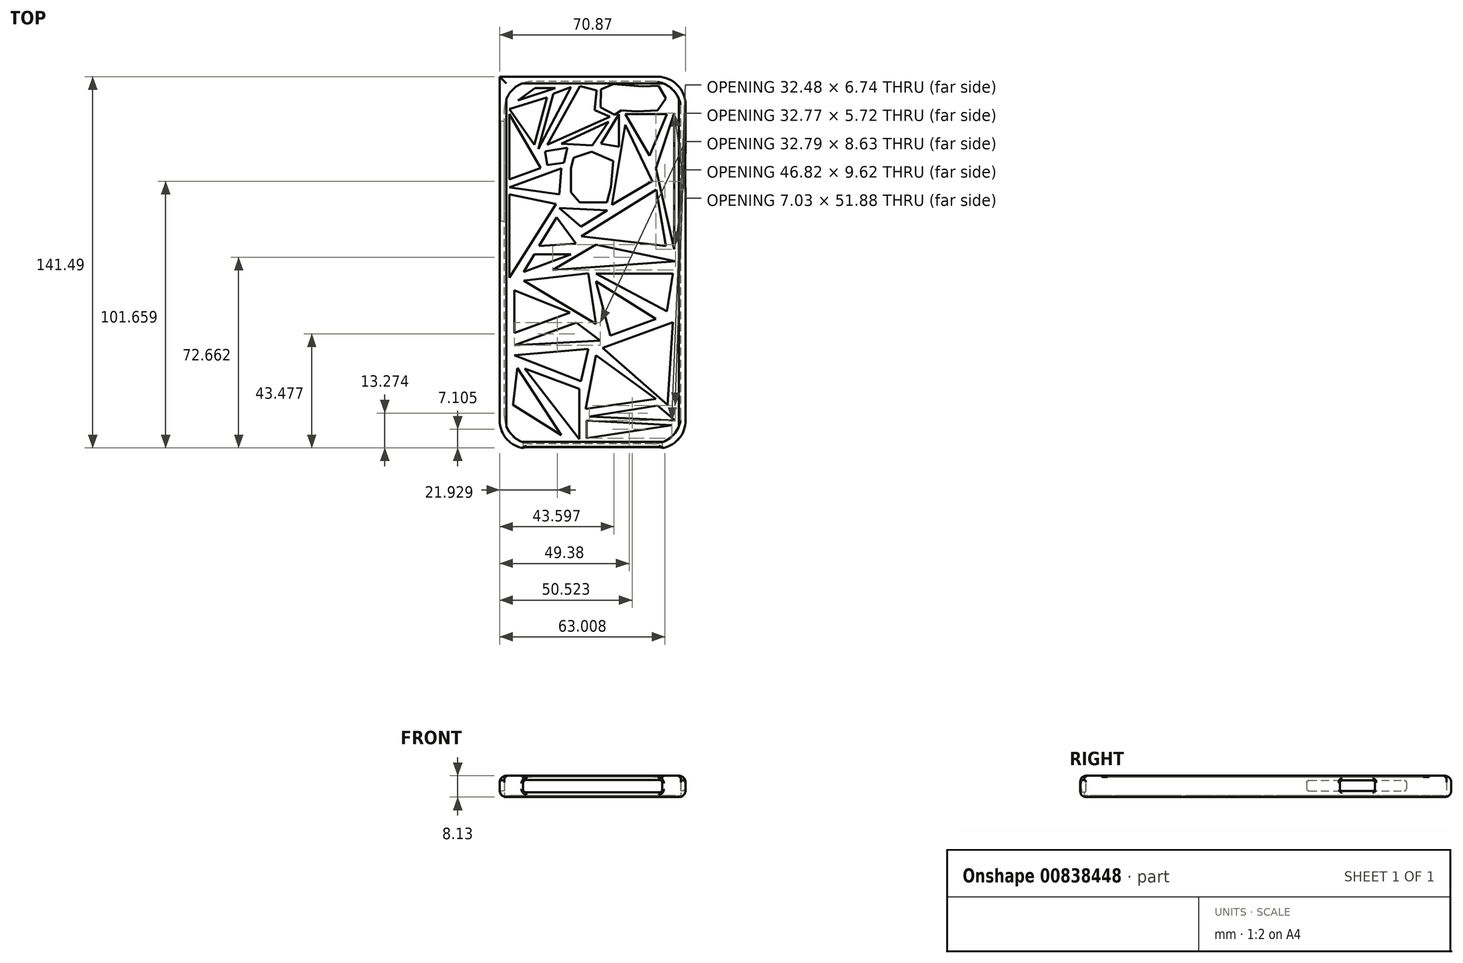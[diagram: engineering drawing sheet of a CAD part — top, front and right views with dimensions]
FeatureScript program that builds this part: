
annotation { "Feature Type Name" : "Feature", "Feature Type Description" : "" }
export const myFeature = defineFeature(function(context is Context, id is Id, definition is map)
    precondition{}
    {
        {
            var Q0;
            Q0=qCreatedBy(makeId("Top.planeOp"),FACE);
            var sketch = newSketch(context, id + "F0", { "sketchPlane" : qUnion([Q0])});
            skLineSegment(sketch, "E0.bottom", {"start": v(0, 0) * mm, "end": v(70.87, 0) * mm});
            skLineSegment(sketch, "E0.top", {"start": v(0, -141.73) * mm, "end": v(70.87, -141.73) * mm});
            skLineSegment(sketch, "E0.left", {"start": v(0, 0) * mm, "end": v(0, -141.73) * mm});
            skLineSegment(sketch, "E0.right", {"start": v(70.87, 0) * mm, "end": v(70.87, -141.73) * mm});
            skLineSegment(sketch, "E1.bottom", {"start": v(0, 0) * mm, "end": v(66.75, 0) * mm});
            skLineSegment(sketch, "E1.left", {"start": v(0, 0) * mm, "end": v(0, -137.57) * mm});
            skLineSegment(sketch, "E2.bottom", {"start": v(69.09, -139.95) * mm, "end": v(1.78, -139.95) * mm});
            skLineSegment(sketch, "E2.top", {"start": v(69.09, -1.78) * mm, "end": v(1.78, -1.78) * mm});
            skLineSegment(sketch, "E2.left", {"start": v(69.09, -139.95) * mm, "end": v(69.09, -1.78) * mm});
            skLineSegment(sketch, "E2.right", {"start": v(1.78, -139.95) * mm, "end": v(1.78, -1.78) * mm});
            skPoint(sketch, "E2.middle", {"position": v(35.43, -70.87) * mm});
            skLineSegment(sketch, "E3.0", {"start": v(21.2, -4.27) * mm, "end": v(7, -8.96) * mm});
            skLineSegment(sketch, "E3.1", {"start": v(7, -8.96) * mm, "end": v(13.43, -4.27) * mm});
            skLineSegment(sketch, "E3.2", {"start": v(13.43, -4.27) * mm, "end": v(21.2, -4.27) * mm});
            skPoint(sketch, "E3.0.midPoint", {"position": v(14.1, -6.62) * mm});
            skLineSegment(sketch, "E4", {"start": v(3.66, -12.3) * mm, "end": v(17.98, -7.89) * mm});
            skLineSegment(sketch, "E5", {"start": v(17.98, -7.89) * mm, "end": v(13.16, -25.95) * mm});
            skLineSegment(sketch, "E6", {"start": v(13.16, -25.95) * mm, "end": v(3.66, -12.3) * mm});
            skLineSegment(sketch, "E7", {"start": v(3.66, -14.2) * mm, "end": v(3.66, -39.11) * mm});
            skLineSegment(sketch, "E8", {"start": v(3.66, -39.11) * mm, "end": v(15.66, -34.74) * mm});
            skLineSegment(sketch, "E9", {"start": v(15.66, -34.74) * mm, "end": v(3.66, -14.2) * mm});
            skLineSegment(sketch, "E10", {"start": v(14.77, -27.56) * mm, "end": v(20.4, -6.45) * mm});
            skLineSegment(sketch, "E11", {"start": v(20.4, -6.45) * mm, "end": v(27.18, -3.98) * mm});
            skLineSegment(sketch, "E12", {"start": v(27.18, -3.98) * mm, "end": v(14.77, -27.56) * mm});
            skLineSegment(sketch, "E13", {"start": v(23.44, -25.52) * mm, "end": v(35.27, -26.22) * mm});
            skLineSegment(sketch, "E14", {"start": v(35.27, -26.22) * mm, "end": v(41.5, -17.2) * mm});
            skLineSegment(sketch, "E15", {"start": v(41.5, -17.2) * mm, "end": v(23.44, -25.52) * mm});
            skLineSegment(sketch, "E16", {"start": v(45.4, -14.2) * mm, "end": v(45.4, -26.67) * mm});
            skLineSegment(sketch, "E17", {"start": v(45.4, -26.67) * mm, "end": v(38.58, -25.58) * mm});
            skLineSegment(sketch, "E18", {"start": v(38.58, -25.58) * mm, "end": v(45.4, -14.2) * mm});
            skLineSegment(sketch, "E19", {"start": v(47.85, -14.2) * mm, "end": v(57.17, -30.16) * mm});
            skLineSegment(sketch, "E20", {"start": v(57.17, -30.16) * mm, "end": v(63.8, -14.25) * mm});
            skLineSegment(sketch, "E21", {"start": v(63.8, -14.25) * mm, "end": v(47.85, -14.2) * mm});
            skLineSegment(sketch, "E22", {"start": v(47.85, -18.22) * mm, "end": v(42.74, -48.7) * mm});
            skLineSegment(sketch, "E23", {"start": v(42.74, -48.7) * mm, "end": v(58.17, -39.69) * mm});
            skLineSegment(sketch, "E24", {"start": v(58.17, -39.69) * mm, "end": v(47.85, -18.22) * mm});
            skLineSegment(sketch, "E25", {"start": v(59.5, -34.98) * mm, "end": v(66.53, -65.77) * mm});
            skLineSegment(sketch, "E26", {"start": v(66.53, -65.77) * mm, "end": v(66.53, -13.9) * mm});
            skLineSegment(sketch, "E27", {"start": v(66.53, -13.9) * mm, "end": v(59.5, -34.98) * mm});
            skLineSegment(sketch, "E28", {"start": v(59.62, -43.08) * mm, "end": v(31.16, -60.86) * mm});
            skLineSegment(sketch, "E29", {"start": v(31.16, -60.86) * mm, "end": v(63.41, -64.56) * mm});
            skLineSegment(sketch, "E30", {"start": v(63.41, -64.56) * mm, "end": v(59.62, -43.08) * mm});
            skLineSegment(sketch, "E31", {"start": v(23.44, -34.98) * mm, "end": v(3.66, -42.2) * mm});
            skLineSegment(sketch, "E32", {"start": v(3.66, -42.2) * mm, "end": v(22.67, -44.83) * mm});
            skLineSegment(sketch, "E33", {"start": v(22.67, -44.83) * mm, "end": v(23.44, -34.98) * mm});
            skLineSegment(sketch, "E34", {"start": v(3.66, -44.83) * mm, "end": v(3.66, -76.54) * mm});
            skLineSegment(sketch, "E35", {"start": v(3.66, -76.54) * mm, "end": v(21.46, -48.57) * mm});
            skLineSegment(sketch, "E36", {"start": v(21.46, -48.57) * mm, "end": v(3.66, -44.83) * mm});
            skLineSegment(sketch, "E37", {"start": v(27.18, -67.68) * mm, "end": v(13.21, -67.68) * mm});
            skLineSegment(sketch, "E38", {"start": v(13.21, -67.68) * mm, "end": v(9.15, -74.46) * mm});
            skLineSegment(sketch, "E39", {"start": v(9.15, -74.46) * mm, "end": v(27.18, -67.68) * mm});
            skLineSegment(sketch, "E40", {"start": v(36.66, -64.02) * mm, "end": v(20.19, -73.64) * mm});
            skLineSegment(sketch, "E41", {"start": v(20.19, -73.64) * mm, "end": v(67, -70.4) * mm});
            skLineSegment(sketch, "E42", {"start": v(67, -70.4) * mm, "end": v(36.66, -64.02) * mm});
            skLineSegment(sketch, "E43", {"start": v(63.76, -89.4) * mm, "end": v(36.76, -75.11) * mm});
            skLineSegment(sketch, "E44", {"start": v(36.76, -75.11) * mm, "end": v(65.98, -75.11) * mm});
            skLineSegment(sketch, "E45", {"start": v(63.76, -89.4) * mm, "end": v(65.98, -75.11) * mm});
            skLineSegment(sketch, "E46", {"start": v(36.75, -77.91) * mm, "end": v(59.5, -92.38) * mm});
            skLineSegment(sketch, "E47", {"start": v(59.5, -92.38) * mm, "end": v(42.21, -98.68) * mm});
            skLineSegment(sketch, "E48", {"start": v(42.21, -98.68) * mm, "end": v(36.75, -77.91) * mm});
            skLineSegment(sketch, "E49", {"start": v(33.77, -74.94) * mm, "end": v(9.15, -77.75) * mm});
            skLineSegment(sketch, "E50", {"start": v(9.15, -77.75) * mm, "end": v(36.75, -94.26) * mm});
            skLineSegment(sketch, "E51", {"start": v(36.75, -94.26) * mm, "end": v(33.77, -74.94) * mm});
            skLineSegment(sketch, "E52", {"start": v(5.53, -81.36) * mm, "end": v(5.53, -97.7) * mm});
            skLineSegment(sketch, "E53", {"start": v(5.53, -97.7) * mm, "end": v(26.84, -89.93) * mm});
            skLineSegment(sketch, "E54", {"start": v(26.84, -89.93) * mm, "end": v(5.53, -81.36) * mm});
            skLineSegment(sketch, "E55", {"start": v(29.2, -93.7) * mm, "end": v(5.53, -102.33) * mm});
            skLineSegment(sketch, "E56", {"start": v(5.53, -102.33) * mm, "end": v(38.32, -100.63) * mm});
            skLineSegment(sketch, "E57", {"start": v(38.32, -100.63) * mm, "end": v(29.2, -93.7) * mm});
            skLineSegment(sketch, "E58", {"start": v(65.98, -93.63) * mm, "end": v(39.3, -103.36) * mm});
            skLineSegment(sketch, "E59", {"start": v(39.3, -103.36) * mm, "end": v(64.02, -125.13) * mm});
            skLineSegment(sketch, "E60", {"start": v(64.02, -125.13) * mm, "end": v(65.98, -93.63) * mm});
            skLineSegment(sketch, "E61", {"start": v(36.75, -106.12) * mm, "end": v(32.81, -126.58) * mm});
            skLineSegment(sketch, "E62", {"start": v(32.81, -126.58) * mm, "end": v(59.5, -122.77) * mm});
            skLineSegment(sketch, "E63", {"start": v(59.5, -122.77) * mm, "end": v(36.75, -106.12) * mm});
            skLineSegment(sketch, "E64", {"start": v(60.13, -125.36) * mm, "end": v(34.14, -129.48) * mm});
            skLineSegment(sketch, "E65", {"start": v(34.14, -129.48) * mm, "end": v(66.9, -131.07) * mm});
            skLineSegment(sketch, "E66", {"start": v(66.9, -131.07) * mm, "end": v(60.13, -125.36) * mm});
            skLineSegment(sketch, "E67", {"start": v(33.77, -103.71) * mm, "end": v(5.53, -106.12) * mm});
            skLineSegment(sketch, "E68", {"start": v(5.53, -106.12) * mm, "end": v(31.04, -116.01) * mm});
            skLineSegment(sketch, "E69", {"start": v(31.04, -116.01) * mm, "end": v(33.77, -103.71) * mm});
            skLineSegment(sketch, "E70", {"start": v(6.74, -110.94) * mm, "end": v(5.12, -125.08) * mm});
            skLineSegment(sketch, "E71", {"start": v(5.12, -125.08) * mm, "end": v(23.44, -136.7) * mm});
            skLineSegment(sketch, "E72", {"start": v(23.44, -136.7) * mm, "end": v(6.74, -110.94) * mm});
            skLineSegment(sketch, "E73", {"start": v(9.52, -111.2) * mm, "end": v(30.36, -138.16) * mm});
            skLineSegment(sketch, "E74", {"start": v(30.36, -138.16) * mm, "end": v(30.36, -118.96) * mm});
            skLineSegment(sketch, "E75", {"start": v(30.36, -118.96) * mm, "end": v(9.52, -111.2) * mm});
            skPoint(sketch, "E76.middle", {"position": v(51.66, -7.81) * mm});
            skPoint(sketch, "E76.middle.positionSnap0", {"position": v(53.2, -9.7) * mm});
            skPoint(sketch, "E76.centerSnap0", {"position": v(51.66, -10.15) * mm});
            skLineSegment(sketch, "E77", {"start": v(30.6, -3.5) * mm, "end": v(18.11, -25.94) * mm});
            skLineSegment(sketch, "E78", {"start": v(18.11, -25.94) * mm, "end": v(41.99, -15.27) * mm});
            skLineSegment(sketch, "E79", {"start": v(41.99, -15.27) * mm, "end": v(36.18, -12.73) * mm});
            skLineSegment(sketch, "E80", {"start": v(36.18, -12.73) * mm, "end": v(36.9, -5.25) * mm});
            skLineSegment(sketch, "E81", {"start": v(36.9, -5.25) * mm, "end": v(30.6, -3.5) * mm});
            skLineSegment(sketch, "E82", {"start": v(38.56, -4.85) * mm, "end": v(43.3, -2.82) * mm});
            skLineSegment(sketch, "E83", {"start": v(43.3, -2.82) * mm, "end": v(54.53, -3.7) * mm});
            skLineSegment(sketch, "E84", {"start": v(54.53, -3.7) * mm, "end": v(60.52, -3.44) * mm});
            skLineSegment(sketch, "E85", {"start": v(60.52, -3.44) * mm, "end": v(63.38, -8.25) * mm});
            skLineSegment(sketch, "E86", {"start": v(63.38, -8.25) * mm, "end": v(60.18, -12.89) * mm});
            skLineSegment(sketch, "E87", {"start": v(60.18, -12.89) * mm, "end": v(52.28, -13.27) * mm});
            skLineSegment(sketch, "E88", {"start": v(52.28, -13.27) * mm, "end": v(46.4, -12.8) * mm});
            skLineSegment(sketch, "E89", {"start": v(46.4, -12.8) * mm, "end": v(43.82, -14.42) * mm});
            skLineSegment(sketch, "E90", {"start": v(43.82, -14.42) * mm, "end": v(38.46, -11.7) * mm});
            skLineSegment(sketch, "E91", {"start": v(38.46, -11.7) * mm, "end": v(38.56, -4.85) * mm});
            skLineSegment(sketch, "E92", {"start": v(0, -141.73) * mm, "end": v(0, 0) * mm});
            skLineSegment(sketch, "E93", {"start": v(70.87, -34.36) * mm, "end": v(43.69, -34.36) * mm, "construction": true});
            skLineSegment(sketch, "E94", {"start": v(43.69, -34.36) * mm, "end": v(43.69, -28.24) * mm, "construction": true});
            skLineSegment(sketch, "E95", {"start": v(33.38, -28.58) * mm, "end": v(43.69, -28.58) * mm, "construction": true});
            skLineSegment(sketch, "E96", {"start": v(43.69, -28.58) * mm, "end": v(43.69, -47.87) * mm, "construction": true});
            skLineSegment(sketch, "E97", {"start": v(43.69, -47.87) * mm, "end": v(27.18, -47.87) * mm, "construction": true});
            skLineSegment(sketch, "E98", {"start": v(27.18, -47.87) * mm, "end": v(27.18, -28.58) * mm, "construction": true});
            skLineSegment(sketch, "E99", {"start": v(27.18, -28.58) * mm, "end": v(33.38, -28.58) * mm, "construction": true});
            skLineSegment(sketch, "E100", {"start": v(17.23, -28.41) * mm, "end": v(25.81, -27.1) * mm});
            skLineSegment(sketch, "E101", {"start": v(25.81, -27.1) * mm, "end": v(24.5, -32.7) * mm});
            skLineSegment(sketch, "E102", {"start": v(24.5, -32.7) * mm, "end": v(18.1, -33.67) * mm});
            skLineSegment(sketch, "E103", {"start": v(18.1, -33.67) * mm, "end": v(17.23, -28.41) * mm});
            skLineSegment(sketch, "E104", {"start": v(41.06, -50.92) * mm, "end": v(22.75, -50.05) * mm});
            skLineSegment(sketch, "E105", {"start": v(22.75, -50.05) * mm, "end": v(30.98, -57.14) * mm});
            skLineSegment(sketch, "E106", {"start": v(30.98, -57.14) * mm, "end": v(41.06, -50.92) * mm});
            skLineSegment(sketch, "E107", {"start": v(27.18, -47.87) * mm, "end": v(27.18, -40.15) * mm});
            skLineSegment(sketch, "E108", {"start": v(27.18, -40.15) * mm, "end": v(27.18, -40.15) * mm});
            skLineSegment(sketch, "E109", {"start": v(27.18, -40.15) * mm, "end": v(27.18, -34.8) * mm});
            skLineSegment(sketch, "E110", {"start": v(27.18, -34.8) * mm, "end": v(27.18, -29.73) * mm});
            skLineSegment(sketch, "E111", {"start": v(35.02, -28.58) * mm, "end": v(43.34, -32.12) * mm});
            skLineSegment(sketch, "E112", {"start": v(43.34, -32.12) * mm, "end": v(42.38, -42.06) * mm});
            skLineSegment(sketch, "E113", {"start": v(42.38, -42.06) * mm, "end": v(40.85, -47.87) * mm});
            skLineSegment(sketch, "E114", {"start": v(40.85, -47.87) * mm, "end": v(30.42, -47.87) * mm});
            skLineSegment(sketch, "E115", {"start": v(30.42, -47.87) * mm, "end": v(27.18, -44.01) * mm});
            skLineSegment(sketch, "E116", {"start": v(27.18, -44.01) * mm, "end": v(28.5, -38.82) * mm});
            skLineSegment(sketch, "E117", {"start": v(28.5, -38.82) * mm, "end": v(27.18, -34.8) * mm});
            skLineSegment(sketch, "E118", {"start": v(27.18, -34.8) * mm, "end": v(28.23, -30.8) * mm});
            skLineSegment(sketch, "E119", {"start": v(28.23, -30.8) * mm, "end": v(35.02, -28.58) * mm});
            skLineSegment(sketch, "E120", {"start": v(21.74, -53.61) * mm, "end": v(15.04, -64.55) * mm});
            skLineSegment(sketch, "E121", {"start": v(15.04, -64.55) * mm, "end": v(29.03, -63.67) * mm});
            skLineSegment(sketch, "E122", {"start": v(29.03, -63.67) * mm, "end": v(21.74, -53.61) * mm});
            skLineSegment(sketch, "E123", {"start": v(33.14, -131.01) * mm, "end": v(33.14, -137.76) * mm});
            skLineSegment(sketch, "E124", {"start": v(33.14, -137.76) * mm, "end": v(65.62, -132.8) * mm});
            skLineSegment(sketch, "E125", {"start": v(65.62, -132.8) * mm, "end": v(33.14, -131.01) * mm});
            skSolve(sketch);
        }
        {
            var Q0;
            Q0 = qSketchRegion(id + "F0", true);
            extrude(context, id + "F1", {"entities" : qUnion([Q0]), "depth" : 7.62 * mm, "offsetDistance" : 25.4 * mm});
        }
        {
            var Q0;
            Q0=makeQuery(id+"F1.opExtrude","SWEPT_EDGE",EDGE,{"disambiguationData":[OSD([sQuery(id+"F0.wireOp",EDGE,"E2.top"),sQuery(id+"F0.wireOp",EDGE,"E2.right")])]});
            var Q1;
            Q1=makeQuery(id+"F1.opExtrude","SWEPT_EDGE",EDGE,{"disambiguationData":[OSD([sQuery(id+"F0.wireOp",EDGE,"E2.top"),sQuery(id+"F0.wireOp",EDGE,"E2.left")])]});
            var Q2;
            Q2=makeQuery(id+"F1.opExtrude","SWEPT_EDGE",EDGE,{"disambiguationData":[OSD([sQuery(id+"F0.wireOp",EDGE,"E2.bottom"),sQuery(id+"F0.wireOp",EDGE,"E2.left")])]});
            var Q3;
            Q3=makeQuery(id+"F1.opExtrude","SWEPT_EDGE",EDGE,{"disambiguationData":[OSD([sQuery(id+"F0.wireOp",EDGE,"E2.bottom"),sQuery(id+"F0.wireOp",EDGE,"E2.right")])]});
            fillet(context, id + "F2", {"entities" : qUnion([Q0, Q1, Q2, Q3]), "radius" : 10.67 * mm, "tangentPropagation" : true, "allowEdgeOverflow" : false});
        }
        {
            var Q0;
            Q0=makeQuery(id+"F1.opExtrude","SWEPT_EDGE",EDGE,{"disambiguationData":[OSD([sQuery(id+"F0.wireOp",EDGE,"E1.bottom"),sQuery(id+"F0.wireOp",EDGE,"E1.left")])]});
            var Q1;
            Q1=makeQuery(id+"F1.opExtrude","SWEPT_EDGE",EDGE,{"disambiguationData":[OSD([sQuery(id+"F0.wireOp",EDGE,"E0.bottom"),sQuery(id+"F0.wireOp",EDGE,"E0.right")])]});
            var Q2;
            Q2=makeQuery(id+"F1.opExtrude","SWEPT_EDGE",EDGE,{"disambiguationData":[OSD([sQuery(id+"F0.wireOp",EDGE,"E0.top"),sQuery(id+"F0.wireOp",EDGE,"E0.right")])]});
            var Q3;
            Q3=makeQuery(id+"F1.opExtrude","SWEPT_EDGE",EDGE,{"disambiguationData":[OSD([sQuery(id+"F0.wireOp",EDGE,"E0.top"),sQuery(id+"F0.wireOp",EDGE,"E0.left")])]});
            fillet(context, id + "F3", {"entities" : qUnion([Q0, Q1, Q2, Q3]), "radius" : 10.67 * mm, "tangentPropagation" : true, "allowEdgeOverflow" : false});
        }
        {
            var Q0;
            Q0=qCreatedBy(makeId("Right.planeOp"),FACE);
            var sketch = newSketch(context, id + "F4", { "sketchPlane" : qUnion([Q0])});
            skLineSegment(sketch, "E126.bottom", {"start": v(-55.17, 6.35) * mm, "end": v(-17.07, 6.35) * mm});
            skLineSegment(sketch, "E126.top", {"start": v(-55.17, 2.35) * mm, "end": v(-17.07, 2.35) * mm});
            skLineSegment(sketch, "E126.left", {"start": v(-55.17, 6.35) * mm, "end": v(-55.17, 2.35) * mm});
            skLineSegment(sketch, "E126.right", {"start": v(-17.07, 6.35) * mm, "end": v(-17.07, 2.35) * mm});
            skPoint(sketch, "E126.middle", {"position": v(-36.12, 4.35) * mm});
            skLineSegment(sketch, "E127", {"start": v(-17.07, 6.35) * mm, "end": v(-55.17, 6.35) * mm});
            skLineSegment(sketch, "E128.bottom", {"start": v(-29.1, 2.35) * mm, "end": v(-42.52, 2.35) * mm});
            skLineSegment(sketch, "E128.top", {"start": v(-29.1, 6.35) * mm, "end": v(-42.52, 6.35) * mm});
            skLineSegment(sketch, "E128.left", {"start": v(-29.1, 2.35) * mm, "end": v(-29.1, 6.35) * mm});
            skLineSegment(sketch, "E128.right", {"start": v(-42.52, 2.35) * mm, "end": v(-42.52, 6.35) * mm});
            skPoint(sketch, "E128.middle", {"position": v(-35.81, 4.35) * mm});
            skLineSegment(sketch, "E129", {"start": v(-32, 0) * mm, "end": v(-38.19, 0) * mm, "construction": true});
            skSolve(sketch);
        }
        {
            var Q0;
            {var subQ2=sQuery(id+"F4.wireOp",EDGE,"E128.left");Q0=makeQuery(id+"F4.imprint","IMPRINT",FACE,{"disambiguationData":[TD([[makeQuery(id+"F4.imprint","IMPRINT",EDGE,{"derivedFrom":subQ2}),1.0]])]});}
            extrude(context, id + "F5", {"entities" : qUnion([Q0]), "operationType" : NewBodyOperationType.REMOVE, "oppositeDirection" : true, "depth" : -76.2 * mm, "offsetDistance" : 25.4 * mm});
        }
        {
            var Q0;
            {var subQ0=sQuery(id+"F4.wireOp",EDGE,"E126.right");Q0=makeQuery(id+"F4.imprint","IMPRINT",FACE,{"disambiguationData":[TD([[makeQuery(id+"F4.imprint","IMPRINT",EDGE,{"derivedFrom":subQ0}),-1.0]])]});}
            var Q1;
            {var subQ2=sQuery(id+"F4.wireOp",EDGE,"E126.left");Q1=makeQuery(id+"F4.imprint","IMPRINT",FACE,{"disambiguationData":[TD([[makeQuery(id+"F4.imprint","IMPRINT",EDGE,{"derivedFrom":subQ2}),1.0]])]});}
            extrude(context, id + "F6", {"entities" : qUnion([Q0, Q1]), "operationType" : NewBodyOperationType.REMOVE, "oppositeDirection" : true, "depth" : -1.78 * mm, "offsetDistance" : 25.4 * mm});
        }
        {
            var Q0;
            Q0=makeQuery(id+"F6.boolean.opBoolean","COPY",EDGE,{"derivedFrom":makeQuery(id+"F6.opExtrude","SWEPT_EDGE",EDGE,{"disambiguationData":[OSD([sQuery(id+"F4.wireOp",EDGE,"E126.top"),sQuery(id+"F4.wireOp",EDGE,"E126.right")])]})});
            var Q1;
            Q1=makeQuery(id+"F6.boolean.opBoolean","COPY",EDGE,{"derivedFrom":makeQuery(id+"F6.opExtrude","SWEPT_EDGE",EDGE,{"disambiguationData":[OSD([sQuery(id+"F4.wireOp",EDGE,"E126.bottom"),sQuery(id+"F4.wireOp",EDGE,"E126.right")])]})});
            var Q2;
            Q2=makeQuery(id+"F6.boolean.opBoolean","COPY",EDGE,{"derivedFrom":makeQuery(id+"F6.opExtrude","SWEPT_EDGE",EDGE,{"disambiguationData":[OSD([sQuery(id+"F4.wireOp",EDGE,"E126.bottom"),sQuery(id+"F4.wireOp",EDGE,"E126.left")])]})});
            var Q3;
            Q3=makeQuery(id+"F6.boolean.opBoolean","COPY",EDGE,{"derivedFrom":makeQuery(id+"F6.opExtrude","SWEPT_EDGE",EDGE,{"disambiguationData":[OSD([sQuery(id+"F4.wireOp",EDGE,"E126.top"),sQuery(id+"F4.wireOp",EDGE,"E126.left")])]})});
            var Q4;
            {var subQ0=sQuery(id+"F4.wireOp",EDGE,"E126.top");var subQ1=sQuery(id+"F4.wireOp",EDGE,"E128.right");Q4=makeQuery(id+"F5.boolean.opBoolean","COPY",EDGE,{"disambiguationData":[TD([makeQuery(id+"F1.opExtrude","SWEPT_FACE",FACE,{"disambiguationData":[OSD([sQuery(id+"F0.wireOp",EDGE,"E0.right")])]})])],"derivedFrom":makeQuery(id+"F5.opExtrude","SWEPT_EDGE",EDGE,{"disambiguationData":[OSD([subQ0,subQ1])]})});}
            var Q5;
            {var subQ0=sQuery(id+"F4.wireOp",EDGE,"E126.top");var subQ1=sQuery(id+"F4.wireOp",EDGE,"E128.left");Q5=makeQuery(id+"F5.boolean.opBoolean","COPY",EDGE,{"disambiguationData":[TD([makeQuery(id+"F1.opExtrude","SWEPT_FACE",FACE,{"disambiguationData":[OSD([sQuery(id+"F0.wireOp",EDGE,"E0.right")])]})])],"derivedFrom":makeQuery(id+"F5.opExtrude","SWEPT_EDGE",EDGE,{"disambiguationData":[OSD([subQ0,subQ1])]})});}
            var Q6;
            {var subQ0=sQuery(id+"F4.wireOp",EDGE,"E126.bottom");var subQ1=sQuery(id+"F4.wireOp",EDGE,"E128.left");Q6=makeQuery(id+"F5.boolean.opBoolean","COPY",EDGE,{"disambiguationData":[TD([makeQuery(id+"F1.opExtrude","SWEPT_FACE",FACE,{"disambiguationData":[OSD([sQuery(id+"F0.wireOp",EDGE,"E0.right")])]})])],"derivedFrom":makeQuery(id+"F5.opExtrude","SWEPT_EDGE",EDGE,{"disambiguationData":[OSD([subQ0,subQ1])]})});}
            var Q7;
            {var subQ0=sQuery(id+"F4.wireOp",EDGE,"E126.bottom");var subQ1=sQuery(id+"F4.wireOp",EDGE,"E128.right");Q7=makeQuery(id+"F5.boolean.opBoolean","COPY",EDGE,{"disambiguationData":[TD([makeQuery(id+"F1.opExtrude","SWEPT_FACE",FACE,{"disambiguationData":[OSD([sQuery(id+"F0.wireOp",EDGE,"E0.right")])]})])],"derivedFrom":makeQuery(id+"F5.opExtrude","SWEPT_EDGE",EDGE,{"disambiguationData":[OSD([subQ0,subQ1])]})});}
            fillet(context, id + "F7", {"entities" : qUnion([Q0, Q1, Q2, Q3, Q4, Q5, Q6, Q7]), "radius" : 0.92 * mm, "tangentPropagation" : true, "allowEdgeOverflow" : false});
        }
        {
            var Q0;
            Q0=makeQuery(id+"F0.imprint","IMPRINT",FACE,{"disambiguationData":[TD([[makeQuery(id+"F0.imprint","IMPRINT",EDGE,{"derivedFrom":sQuery(id+"F0.wireOp",EDGE,"E2.bottom")}),-1.0]])]});
            extrude(context, id + "F8", {"entities" : qUnion([Q0]), "operationType" : NewBodyOperationType.ADD, "depth" : 0.5 * mm, "offsetDistance" : 25.4 * mm});
        }
        {
            var Q0;
            Q0=makeQuery(id+"F8.opExtrude","SWEPT_EDGE",EDGE,{"disambiguationData":[OSD([sQuery(id+"F0.wireOp",EDGE,"E2.top"),sQuery(id+"F0.wireOp",EDGE,"E2.right")])]});
            var Q1;
            Q1=makeQuery(id+"F8.opExtrude","SWEPT_EDGE",EDGE,{"disambiguationData":[OSD([sQuery(id+"F0.wireOp",EDGE,"E2.bottom"),sQuery(id+"F0.wireOp",EDGE,"E2.right")])]});
            var Q2;
            Q2=makeQuery(id+"F8.opExtrude","SWEPT_EDGE",EDGE,{"disambiguationData":[OSD([sQuery(id+"F0.wireOp",EDGE,"E2.bottom"),sQuery(id+"F0.wireOp",EDGE,"E2.left")])]});
            var Q3;
            Q3=makeQuery(id+"F8.opExtrude","SWEPT_EDGE",EDGE,{"disambiguationData":[OSD([sQuery(id+"F0.wireOp",EDGE,"E2.top"),sQuery(id+"F0.wireOp",EDGE,"E2.left")])]});
            fillet(context, id + "F9", {"entities" : qUnion([Q0, Q1, Q2, Q3]), "radius" : 10.67 * mm, "tangentPropagation" : true, "allowEdgeOverflow" : false});
        }
        {
            var Q0;
            Q0=makeQuery(id+"F1.opExtrude","CAP_EDGE",EDGE,{"disambiguationData":[OSD([sQuery(id+"F0.wireOp",EDGE,"E0.bottom"),sQuery(id+"F0.wireOp",EDGE,"E1.bottom")])],"isStart":true});
            fillet(context, id + "F10", {"entities" : qUnion([Q0]), "radius" : 2.54 * mm, "tangentPropagation" : true, "allowEdgeOverflow" : false});
        }
        {
            var Q0;
            Q0=makeQuery(id+"F1.opExtrude","CAP_FACE",FACE,{"disambiguationData":[OSD([sQuery(id+"F0.wireOp",EDGE,"E0.bottom"),sQuery(id+"F0.wireOp",EDGE,"E0.top"),sQuery(id+"F0.wireOp",EDGE,"E0.left"),sQuery(id+"F0.wireOp",EDGE,"E0.right"),sQuery(id+"F0.wireOp",EDGE,"E1.bottom"),sQuery(id+"F0.wireOp",EDGE,"E1.left"),sQuery(id+"F0.wireOp",EDGE,"E2.bottom"),sQuery(id+"F0.wireOp",EDGE,"E2.top"),sQuery(id+"F0.wireOp",EDGE,"E2.left"),sQuery(id+"F0.wireOp",EDGE,"E2.right")])],"isStart":false});
            var sketch = newSketch(context, id + "F11", { "sketchPlane" : qUnion([Q0])});
            skLineSegment(sketch, "E130.top", {"start": v(108.91, -2.54) * mm, "end": v(108.91, -2.54) * mm});
            skLineSegment(sketch, "E130.left", {"start": v(108.91, -2.54) * mm, "end": v(108.91, -2.54) * mm});
            skPoint(sketch, "E130.middle", {"position": v(108.91, -2.54) * mm});
            skLineSegment(sketch, "E131.bottom", {"start": v(0, 0) * mm, "end": v(70.87, 0) * mm});
            skLineSegment(sketch, "E131.top", {"start": v(0, -141.73) * mm, "end": v(70.87, -141.73) * mm});
            skLineSegment(sketch, "E131.left", {"start": v(0, 0) * mm, "end": v(0, -141.73) * mm});
            skLineSegment(sketch, "E131.right", {"start": v(70.87, 0) * mm, "end": v(70.87, -141.73) * mm});
            skLineSegment(sketch, "E132.bottom", {"start": v(68.33, -139.2) * mm, "end": v(2.54, -139.2) * mm});
            skLineSegment(sketch, "E132.top", {"start": v(68.33, -2.54) * mm, "end": v(2.54, -2.54) * mm});
            skLineSegment(sketch, "E132.left", {"start": v(68.33, -139.2) * mm, "end": v(68.33, -2.54) * mm});
            skLineSegment(sketch, "E132.right", {"start": v(2.54, -139.2) * mm, "end": v(2.54, -2.54) * mm});
            skSolve(sketch);
        }
        {
            var Q0;
            {var subQ0=sQuery(id+"F11.wireOp",EDGE,"E132.top");var subQ1=sQuery(id+"F0.wireOp",EDGE,"E92");var subQ2=sQuery(id+"F0.wireOp",EDGE,"E2.right");var subQ3=sQuery(id+"F0.wireOp",EDGE,"E2.top");var subQ4=sQuery(id+"F0.wireOp",EDGE,"E1.bottom");var subQ5=makeQuery(id+"F1.opExtrude","CAP_FACE",FACE,{"disambiguationData":[OSD([sQuery(id+"F0.wireOp",EDGE,"E0.bottom"),sQuery(id+"F0.wireOp",EDGE,"E0.top"),sQuery(id+"F0.wireOp",EDGE,"E0.right"),subQ4,sQuery(id+"F0.wireOp",EDGE,"E2.bottom"),subQ3,sQuery(id+"F0.wireOp",EDGE,"E2.left"),subQ2,subQ1])],"isStart":false});var subQ6=makeQuery(id+"F2.opFillet","BLEND_EDGE",EDGE,{"blendedFrom":[makeQuery(id+"F1.opExtrude","SWEPT_EDGE",EDGE,{"disambiguationData":[OSD([subQ3,subQ2])]}),subQ5],"blendedInto":[subQ5]});var subQ7=makeQuery(id+"F11.imprint","INTERSECT",VERTEX,{"derivedFrom":[subQ6,subQ0]});Q0=makeQuery(id+"F11.imprint","IMPRINT",FACE,{"disambiguationData":[TD([[makeQuery(id+"F11.imprint","IMPRINT",EDGE,{"disambiguationData":[TD([[subQ7,-1.0]])],"derivedFrom":subQ0}),1.0]])]});}
            var Q1;
            {var subQ0=sQuery(id+"F0.wireOp",EDGE,"E2.right");var subQ1=makeQuery(id+"F1.opExtrude","CAP_EDGE",EDGE,{"disambiguationData":[OSD([subQ0])],"isStart":false});Q1=makeQuery(id+"F11.imprint","IMPRINT",FACE,{"disambiguationData":[TD([[makeQuery(id+"F11.imprint","IMPRINT",EDGE,{"derivedFrom":subQ1}),1.0]])]});}
            var Q2;
            {var subQ4=sQuery(id+"F0.wireOp",EDGE,"E2.top");var subQ14=makeQuery(id+"F1.opExtrude","CAP_EDGE",EDGE,{"disambiguationData":[OSD([subQ4])],"isStart":false});Q2=makeQuery(id+"F11.imprint","IMPRINT",FACE,{"disambiguationData":[TD([[makeQuery(id+"F11.imprint","IMPRINT",EDGE,{"derivedFrom":subQ14}),-1.0]])]});}
            var Q3;
            {var subQ0=sQuery(id+"F0.wireOp",EDGE,"E2.left");var subQ1=makeQuery(id+"F1.opExtrude","CAP_EDGE",EDGE,{"disambiguationData":[OSD([subQ0])],"isStart":false});Q3=makeQuery(id+"F11.imprint","IMPRINT",FACE,{"disambiguationData":[TD([[makeQuery(id+"F11.imprint","IMPRINT",EDGE,{"derivedFrom":subQ1}),-1.0]])]});}
            var Q4;
            {var subQ1=sQuery(id+"F0.wireOp",EDGE,"E2.left");var subQ9=makeQuery(id+"F1.opExtrude","CAP_EDGE",EDGE,{"disambiguationData":[OSD([subQ1])],"isStart":false});Q4=makeQuery(id+"F11.imprint","IMPRINT",FACE,{"disambiguationData":[TD([[makeQuery(id+"F11.imprint","IMPRINT",EDGE,{"derivedFrom":subQ9}),1.0]])]});}
            var Q5;
            {var subQ0=sQuery(id+"F11.wireOp",EDGE,"E132.bottom");var subQ1=sQuery(id+"F0.wireOp",EDGE,"E2.left");var subQ2=sQuery(id+"F0.wireOp",EDGE,"E2.bottom");var subQ3=sQuery(id+"F0.wireOp",EDGE,"E0.right");var subQ4=sQuery(id+"F0.wireOp",EDGE,"E0.top");var subQ5=makeQuery(id+"F1.opExtrude","CAP_FACE",FACE,{"disambiguationData":[OSD([sQuery(id+"F0.wireOp",EDGE,"E0.bottom"),subQ4,subQ3,sQuery(id+"F0.wireOp",EDGE,"E1.bottom"),subQ2,sQuery(id+"F0.wireOp",EDGE,"E2.top"),subQ1,sQuery(id+"F0.wireOp",EDGE,"E2.right"),sQuery(id+"F0.wireOp",EDGE,"E92")])],"isStart":false});var subQ6=makeQuery(id+"F3.opFillet","BLEND_EDGE",EDGE,{"blendedFrom":[makeQuery(id+"F1.opExtrude","SWEPT_EDGE",EDGE,{"disambiguationData":[OSD([subQ4,subQ3])]}),subQ5],"blendedInto":[subQ5]});var subQ7=makeQuery(id+"F11.imprint","INTERSECT",VERTEX,{"derivedFrom":[subQ6,subQ0]});Q5=makeQuery(id+"F11.imprint","IMPRINT",FACE,{"disambiguationData":[TD([[makeQuery(id+"F11.imprint","IMPRINT",EDGE,{"disambiguationData":[TD([[subQ7,-1.0]])],"derivedFrom":subQ0}),-1.0]])]});}
            var Q6;
            {var subQ0=sQuery(id+"F0.wireOp",EDGE,"E2.bottom");var subQ1=makeQuery(id+"F1.opExtrude","CAP_EDGE",EDGE,{"disambiguationData":[OSD([subQ0])],"isStart":false});Q6=makeQuery(id+"F11.imprint","IMPRINT",FACE,{"disambiguationData":[TD([[makeQuery(id+"F11.imprint","IMPRINT",EDGE,{"derivedFrom":subQ1}),1.0]])]});}
            var Q7;
            {var subQ3=sQuery(id+"F0.wireOp",EDGE,"E2.bottom");var subQ9=makeQuery(id+"F1.opExtrude","CAP_EDGE",EDGE,{"disambiguationData":[OSD([subQ3])],"isStart":false});Q7=makeQuery(id+"F11.imprint","IMPRINT",FACE,{"disambiguationData":[TD([[makeQuery(id+"F11.imprint","IMPRINT",EDGE,{"derivedFrom":subQ9}),-1.0]])]});}
            var Q8;
            {var subQ0=sQuery(id+"F11.wireOp",EDGE,"E132.bottom");var subQ1=sQuery(id+"F0.wireOp",EDGE,"E92");var subQ2=sQuery(id+"F0.wireOp",EDGE,"E2.right");var subQ3=sQuery(id+"F0.wireOp",EDGE,"E2.bottom");var subQ4=sQuery(id+"F0.wireOp",EDGE,"E0.top");var subQ5=makeQuery(id+"F1.opExtrude","CAP_FACE",FACE,{"disambiguationData":[OSD([sQuery(id+"F0.wireOp",EDGE,"E0.bottom"),subQ4,sQuery(id+"F0.wireOp",EDGE,"E0.right"),sQuery(id+"F0.wireOp",EDGE,"E1.bottom"),subQ3,sQuery(id+"F0.wireOp",EDGE,"E2.top"),sQuery(id+"F0.wireOp",EDGE,"E2.left"),subQ2,subQ1])],"isStart":false});var subQ6=makeQuery(id+"F2.opFillet","BLEND_EDGE",EDGE,{"blendedFrom":[makeQuery(id+"F1.opExtrude","SWEPT_EDGE",EDGE,{"disambiguationData":[OSD([subQ3,subQ2])]}),subQ5],"blendedInto":[subQ5]});var subQ7=makeQuery(id+"F11.imprint","INTERSECT",VERTEX,{"derivedFrom":[subQ6,subQ0]});Q8=makeQuery(id+"F11.imprint","IMPRINT",FACE,{"disambiguationData":[TD([[makeQuery(id+"F11.imprint","IMPRINT",EDGE,{"disambiguationData":[TD([[subQ7,-1.0]])],"derivedFrom":subQ0}),-1.0]])]});}
            var Q9;
            {var subQ1=sQuery(id+"F0.wireOp",EDGE,"E2.right");var subQ9=makeQuery(id+"F1.opExtrude","CAP_EDGE",EDGE,{"disambiguationData":[OSD([subQ1])],"isStart":false});Q9=makeQuery(id+"F11.imprint","IMPRINT",FACE,{"disambiguationData":[TD([[makeQuery(id+"F11.imprint","IMPRINT",EDGE,{"derivedFrom":subQ9}),-1.0]])]});}
            var Q10;
            {var subQ3=sQuery(id+"F0.wireOp",EDGE,"E2.top");var subQ9=makeQuery(id+"F1.opExtrude","CAP_EDGE",EDGE,{"disambiguationData":[OSD([subQ3])],"isStart":false});Q10=makeQuery(id+"F11.imprint","IMPRINT",FACE,{"disambiguationData":[TD([[makeQuery(id+"F11.imprint","IMPRINT",EDGE,{"derivedFrom":subQ9}),1.0]])]});}
            var Q11;
            {var subQ0=sQuery(id+"F11.wireOp",EDGE,"E132.top");var subQ1=sQuery(id+"F0.wireOp",EDGE,"E2.left");var subQ2=sQuery(id+"F0.wireOp",EDGE,"E2.top");var subQ3=sQuery(id+"F0.wireOp",EDGE,"E0.right");var subQ4=sQuery(id+"F0.wireOp",EDGE,"E0.bottom");var subQ5=makeQuery(id+"F1.opExtrude","CAP_FACE",FACE,{"disambiguationData":[OSD([subQ4,sQuery(id+"F0.wireOp",EDGE,"E0.top"),subQ3,sQuery(id+"F0.wireOp",EDGE,"E1.bottom"),sQuery(id+"F0.wireOp",EDGE,"E2.bottom"),subQ2,subQ1,sQuery(id+"F0.wireOp",EDGE,"E2.right"),sQuery(id+"F0.wireOp",EDGE,"E92")])],"isStart":false});var subQ6=makeQuery(id+"F3.opFillet","BLEND_EDGE",EDGE,{"blendedFrom":[makeQuery(id+"F1.opExtrude","SWEPT_EDGE",EDGE,{"disambiguationData":[OSD([subQ4,subQ3])]}),subQ5],"blendedInto":[subQ5]});var subQ7=makeQuery(id+"F11.imprint","INTERSECT",VERTEX,{"derivedFrom":[subQ6,subQ0]});Q11=makeQuery(id+"F11.imprint","IMPRINT",FACE,{"disambiguationData":[TD([[makeQuery(id+"F11.imprint","IMPRINT",EDGE,{"disambiguationData":[TD([[subQ7,-1.0]])],"derivedFrom":subQ0}),1.0]])]});}
            extrude(context, id + "F12", {"entities" : qUnion([Q0, Q1, Q2, Q3, Q4, Q5, Q6, Q7, Q8, Q9, Q10, Q11]), "operationType" : NewBodyOperationType.ADD, "depth" : 0.5 * mm, "offsetDistance" : 25.4 * mm});
        }
        {
            var Q0;
            Q0=makeQuery(id+"F12.opExtrude","CAP_EDGE",EDGE,{"disambiguationData":[OSD([sQuery(id+"F11.wireOp",EDGE,"E131.left")])],"isStart":false});
            fillet(context, id + "F13", {"entities" : qUnion([Q0]), "radius" : 2.54 * mm, "tangentPropagation" : true, "allowEdgeOverflow" : false});
        }
        {
            var Q0;
            Q0=makeQuery(id+"F12.boolean.opBoolean","MERGE",FACE,{"derivedFrom":[makeQuery(id+"F1.opExtrude","SWEPT_FACE",FACE,{"disambiguationData":[OSD([sQuery(id+"F0.wireOp",EDGE,"E0.top")])]}),makeQuery(id+"F12.opExtrude","SWEPT_FACE",FACE,{"disambiguationData":[OSD([sQuery(id+"F11.wireOp",EDGE,"E131.top")])]})]});
            var sketch = newSketch(context, id + "F14", { "sketchPlane" : qUnion([Q0])});
            skLineSegment(sketch, "E133", {"start": v(0, 2.54) * mm, "end": v(8.89, 2.54) * mm, "construction": true});
            skLineSegment(sketch, "E134", {"start": v(70.9, 3.64) * mm, "end": v(62, 3.64) * mm, "construction": true});
            skLineSegment(sketch, "E135.bottom", {"start": v(62, 1.78) * mm, "end": v(8.9, 1.78) * mm});
            skLineSegment(sketch, "E135.top", {"start": v(62, 6.54) * mm, "end": v(8.9, 6.54) * mm});
            skLineSegment(sketch, "E135.left", {"start": v(62, 1.78) * mm, "end": v(62, 6.54) * mm});
            skLineSegment(sketch, "E135.right", {"start": v(8.89, 1.78) * mm, "end": v(8.89, 6.54) * mm});
            skPoint(sketch, "E135.middle", {"position": v(35.45, 4.16) * mm});
            skSolve(sketch);
        }
        {
            var Q0;
            Q0 = qSketchRegion(id + "F14", true);
            extrude(context, id + "F15", {"entities" : qUnion([Q0]), "operationType" : NewBodyOperationType.REMOVE, "oppositeDirection" : true, "depth" : 25.4 * mm, "offsetDistance" : 25.4 * mm});
        }
        {
            var Q0;
            Q0=makeQuery(id+"F15.boolean.opBoolean","COPY",EDGE,{"derivedFrom":makeQuery(id+"F15.opExtrude","SWEPT_EDGE",EDGE,{"disambiguationData":[OSD([sQuery(id+"F14.wireOp",EDGE,"E135.bottom"),sQuery(id+"F14.wireOp",EDGE,"E135.right")])]})});
            var Q1;
            Q1=makeQuery(id+"F15.boolean.opBoolean","COPY",EDGE,{"derivedFrom":makeQuery(id+"F15.opExtrude","SWEPT_EDGE",EDGE,{"disambiguationData":[OSD([sQuery(id+"F14.wireOp",EDGE,"E135.top"),sQuery(id+"F14.wireOp",EDGE,"E135.right")])]})});
            var Q2;
            Q2=makeQuery(id+"F15.boolean.opBoolean","COPY",EDGE,{"derivedFrom":makeQuery(id+"F15.opExtrude","SWEPT_EDGE",EDGE,{"disambiguationData":[OSD([sQuery(id+"F14.wireOp",EDGE,"E135.bottom"),sQuery(id+"F14.wireOp",EDGE,"E135.left")])]})});
            var Q3;
            Q3=makeQuery(id+"F15.boolean.opBoolean","COPY",EDGE,{"derivedFrom":makeQuery(id+"F15.opExtrude","SWEPT_EDGE",EDGE,{"disambiguationData":[OSD([sQuery(id+"F14.wireOp",EDGE,"E135.top"),sQuery(id+"F14.wireOp",EDGE,"E135.left")])]})});
            fillet(context, id + "F16", {"entities" : qUnion([Q0, Q1, Q2, Q3]), "radius" : 1.27 * mm, "tangentPropagation" : true, "allowEdgeOverflow" : false});
        }
        {
            var Q0;
            {var subQ0=sQuery(id+"F4.wireOp",EDGE,"E126.top");var subQ2=sQuery(id+"F4.wireOp",EDGE,"E128.right");var subQ3=sQuery(id+"F0.wireOp",EDGE,"E92");Q0=makeQuery(id+"F10.opFillet","BLEND_EDGE",EDGE,{"blendedFrom":[makeQuery(id+"F1.opExtrude","CAP_EDGE",EDGE,{"disambiguationData":[OSD([subQ3])],"isStart":true}),makeQuery(id+"F6.boolean.opBoolean","MERGE",FACE,{"derivedFrom":[makeQuery(id+"F5.boolean.opBoolean","COPY",FACE,{"disambiguationData":[TD([makeQuery(id+"F1.opExtrude","SWEPT_FACE",FACE,{"disambiguationData":[OSD([sQuery(id+"F0.wireOp",EDGE,"E2.right")])]})])],"derivedFrom":makeQuery(id+"F5.opExtrude","SWEPT_FACE",FACE,{"disambiguationData":[OSD([subQ0])]})})],"fromTools":[makeQuery(id+"F6.opExtrude","SWEPT_FACE",FACE,{"disambiguationData":[OSD([subQ0]),TDD([makeQuery(id+"F4.imprint","IMPRINT",EDGE,{"disambiguationData":[TD([[makeQuery(id+"F4.imprint","INTERSECT",VERTEX,{"derivedFrom":[subQ0,subQ2]}),1.0]])],"derivedFrom":subQ0})])]}),makeQuery(id+"F6.opExtrude","SWEPT_FACE",FACE,{"disambiguationData":[OSD([subQ0]),TDD([makeQuery(id+"F4.imprint","IMPRINT",EDGE,{"disambiguationData":[TD([[makeQuery(id+"F4.imprint","INTERSECT",VERTEX,{"derivedFrom":[subQ0,sQuery(id+"F4.wireOp",EDGE,"E126.right")]}),1.0]])],"derivedFrom":subQ0})])]})]})],"blendedInto":[makeQuery(id+"F6.boolean.opBoolean","MERGE",FACE,{"derivedFrom":[makeQuery(id+"F5.boolean.opBoolean","COPY",FACE,{"disambiguationData":[TD([makeQuery(id+"F1.opExtrude","SWEPT_FACE",FACE,{"disambiguationData":[OSD([sQuery(id+"F0.wireOp",EDGE,"E2.right")])]})])],"derivedFrom":makeQuery(id+"F5.opExtrude","SWEPT_FACE",FACE,{"disambiguationData":[OSD([subQ0])]})})],"fromTools":[makeQuery(id+"F6.opExtrude","SWEPT_FACE",FACE,{"disambiguationData":[OSD([subQ0]),TDD([makeQuery(id+"F4.imprint","IMPRINT",EDGE,{"disambiguationData":[TD([[makeQuery(id+"F4.imprint","INTERSECT",VERTEX,{"derivedFrom":[subQ0,subQ2]}),1.0]])],"derivedFrom":subQ0})])]}),makeQuery(id+"F6.opExtrude","SWEPT_FACE",FACE,{"disambiguationData":[OSD([subQ0]),TDD([makeQuery(id+"F4.imprint","IMPRINT",EDGE,{"disambiguationData":[TD([[makeQuery(id+"F4.imprint","INTERSECT",VERTEX,{"derivedFrom":[subQ0,sQuery(id+"F4.wireOp",EDGE,"E126.right")]}),1.0]])],"derivedFrom":subQ0})])]})]})]});}
            var Q1;
            Q1=makeQuery(id+"F13.opFillet","BLEND_EDGE",EDGE,{"blendedFrom":[makeQuery(id+"F12.opExtrude","CAP_EDGE",EDGE,{"disambiguationData":[OSD([sQuery(id+"F11.wireOp",EDGE,"E131.right")])],"isStart":false}),makeQuery(id+"F5.boolean.opBoolean","COPY",FACE,{"disambiguationData":[TD([makeQuery(id+"F1.opExtrude","SWEPT_FACE",FACE,{"disambiguationData":[OSD([sQuery(id+"F0.wireOp",EDGE,"E0.right")])]})])],"derivedFrom":makeQuery(id+"F5.opExtrude","SWEPT_FACE",FACE,{"disambiguationData":[OSD([sQuery(id+"F4.wireOp",EDGE,"E126.bottom")])]})})],"blendedInto":[makeQuery(id+"F5.boolean.opBoolean","COPY",FACE,{"disambiguationData":[TD([makeQuery(id+"F1.opExtrude","SWEPT_FACE",FACE,{"disambiguationData":[OSD([sQuery(id+"F0.wireOp",EDGE,"E0.right")])]})])],"derivedFrom":makeQuery(id+"F5.opExtrude","SWEPT_FACE",FACE,{"disambiguationData":[OSD([sQuery(id+"F4.wireOp",EDGE,"E126.bottom")])]})})]});
            var Q2;
            Q2=makeQuery(id+"F15.boolean.opBoolean","INTERSECT",EDGE,{"derivedFrom":[makeQuery(id+"F13.opFillet","BLEND_FACE",FACE,{"disambiguationData":[OSD([sQuery(id+"F11.wireOp",EDGE,"E131.top")])]}),makeQuery(id+"F15.opExtrude","SWEPT_FACE",FACE,{"disambiguationData":[OSD([sQuery(id+"F14.wireOp",EDGE,"E135.top")])]})]});
            fillet(context, id + "F17", {"entities" : qUnion([Q0, Q1, Q2]), "radius" : 0.5 * mm, "tangentPropagation" : true, "allowEdgeOverflow" : false});
        }
    });
